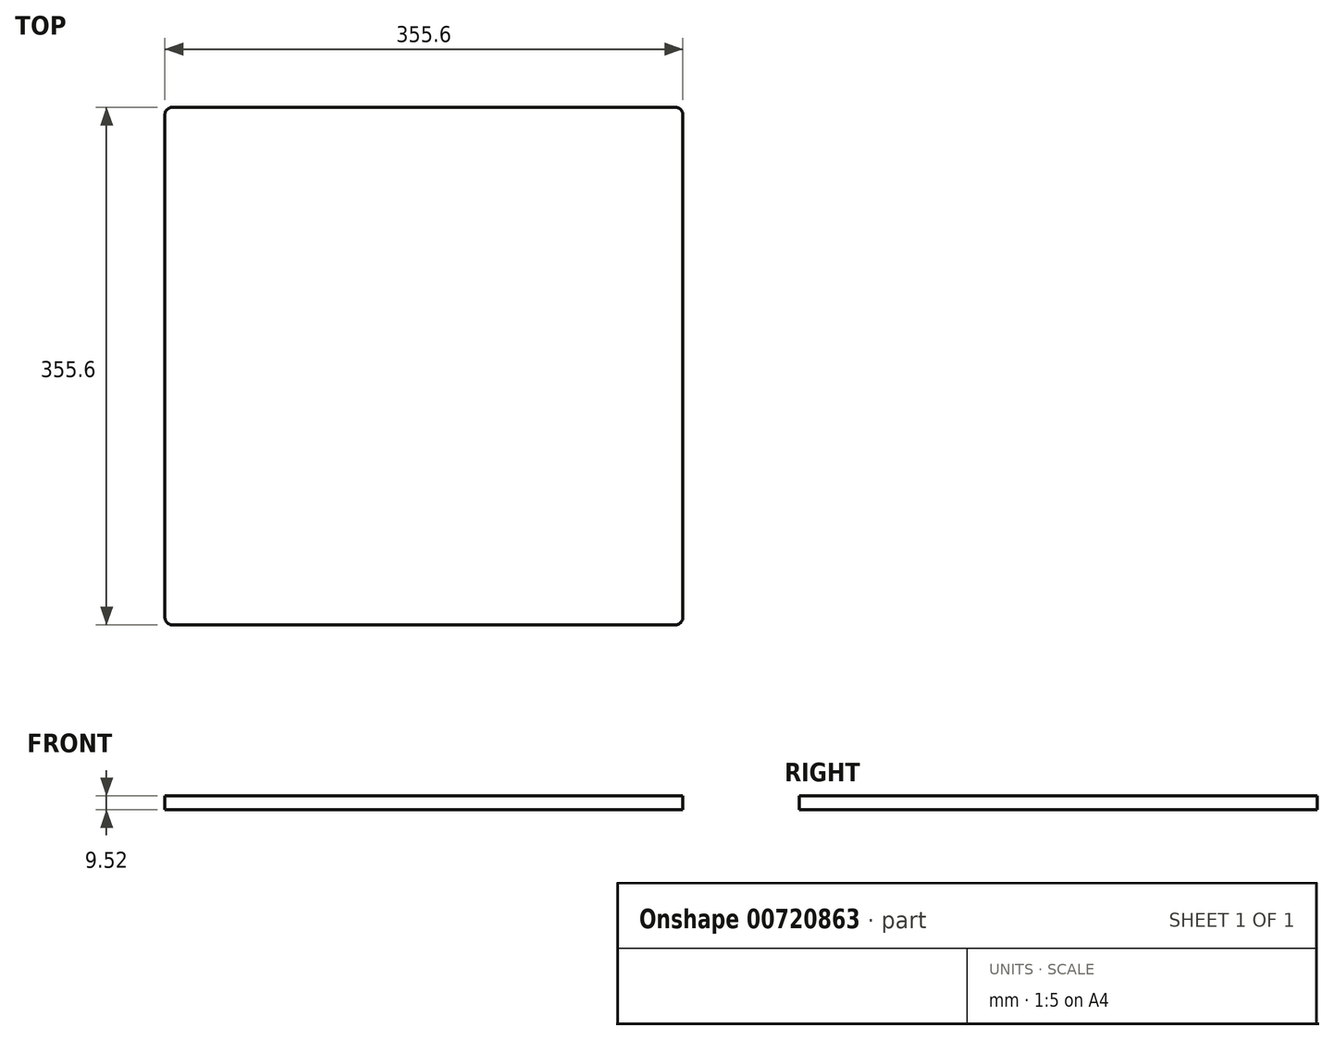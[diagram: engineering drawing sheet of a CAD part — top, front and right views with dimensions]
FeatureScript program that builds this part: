
annotation { "Feature Type Name" : "Feature", "Feature Type Description" : "" }
export const myFeature = defineFeature(function(context is Context, id is Id, definition is map)
    precondition{}
    {
        {
            var Q0;
            Q0=qCreatedBy(makeId("Top.planeOp"),FACE);
            var sketch = newSketch(context, id + "F0", { "sketchPlane" : qUnion([Q0])});
            skLineSegment(sketch, "E0.bottom", {"start": v(-177.8, 177.8) * mm, "end": v(177.8, 177.8) * mm});
            skLineSegment(sketch, "E0.top", {"start": v(-177.8, -177.8) * mm, "end": v(177.8, -177.8) * mm});
            skLineSegment(sketch, "E0.left", {"start": v(-177.8, 177.8) * mm, "end": v(-177.8, -177.8) * mm});
            skLineSegment(sketch, "E0.right", {"start": v(177.8, 177.8) * mm, "end": v(177.8, -177.8) * mm});
            skPoint(sketch, "E0.middle", {"position": v(0, 0) * mm});
            skSolve(sketch);
        }
        {
            var Q0;
            Q0 = qSketchRegion(id + "F0", true);
            extrude(context, id + "F1", {"entities" : qUnion([Q0]), "endBound" : BoundingType.SYMMETRIC, "depth" : 9.52 * mm, "offsetDistance" : 25.4 * mm});
        }
        {
            var Q0;
            Q0=makeQuery(id+"F1.opExtrude","SWEPT_EDGE",EDGE,{"disambiguationData":[OSD([sQuery(id+"F0.wireOp",EDGE,"E0.bottom"),sQuery(id+"F0.wireOp",EDGE,"E0.left")])]});
            var Q1;
            Q1=makeQuery(id+"F1.opExtrude","SWEPT_EDGE",EDGE,{"disambiguationData":[OSD([sQuery(id+"F0.wireOp",EDGE,"E0.top"),sQuery(id+"F0.wireOp",EDGE,"E0.left")])]});
            var Q2;
            Q2=makeQuery(id+"F1.opExtrude","SWEPT_EDGE",EDGE,{"disambiguationData":[OSD([sQuery(id+"F0.wireOp",EDGE,"E0.top"),sQuery(id+"F0.wireOp",EDGE,"E0.right")])]});
            var Q3;
            Q3=makeQuery(id+"F1.opExtrude","SWEPT_EDGE",EDGE,{"disambiguationData":[OSD([sQuery(id+"F0.wireOp",EDGE,"E0.bottom"),sQuery(id+"F0.wireOp",EDGE,"E0.right")])]});
            fillet(context, id + "F2", {"entities" : qUnion([Q0, Q1, Q2, Q3]), "radius" : 5.08 * mm, "tangentPropagation" : true, "allowEdgeOverflow" : false});
        }
    });
